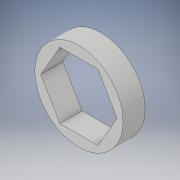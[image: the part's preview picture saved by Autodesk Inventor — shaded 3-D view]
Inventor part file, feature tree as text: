
AUTODESK INVENTOR PART (.ipt)
format: ipt  version: 2018 (Build 220112000, 112)  size: 103,936 bytes
history: native  units: in
note: dims shown in document units (in); Inventor stores cm internally (conversion verified against a paired STEP export)
features: extrude x1, sketch x1
ambient origin geometry x8: Origin, YZ Plane, XZ Plane, XY Plane, X Axis, Y Axis, Z Axis, Center Point
bodies: Solid1 (feature_tree)
feature tree (2):
  extrude  "Extrusion1"  Depth=0.125in
  sketch  "Sketch1"  dims[d0=0.375in d1=0.5in d2=0.125in d3=0.0in]
